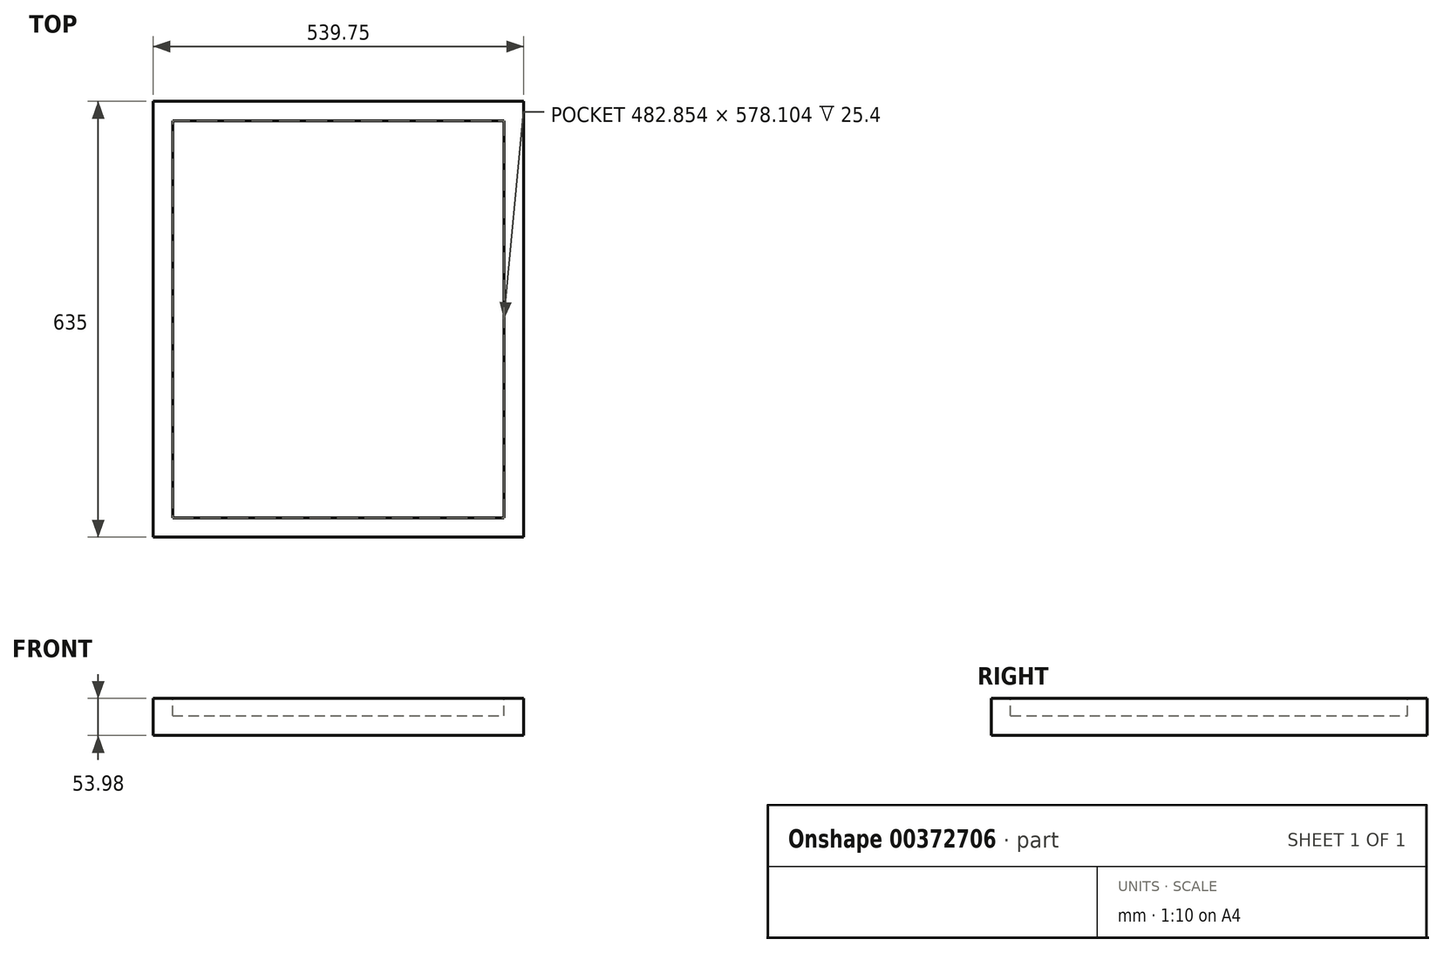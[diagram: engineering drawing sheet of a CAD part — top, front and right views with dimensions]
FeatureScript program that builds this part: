
annotation { "Feature Type Name" : "Feature", "Feature Type Description" : "" }
export const myFeature = defineFeature(function(context is Context, id is Id, definition is map)
    precondition{}
    {
        {
            var Q0;
            Q0=qCreatedBy(makeId("Front.planeOp"),FACE);
            var sketch = newSketch(context, id + "F0", { "sketchPlane" : qUnion([Q0])});
            skLineSegment(sketch, "E0.bottom", {"start": v(0, 0) * mm, "end": v(539.75, 0) * mm});
            skLineSegment(sketch, "E0.top", {"start": v(0, 53.98) * mm, "end": v(539.75, 53.98) * mm});
            skLineSegment(sketch, "E0.left", {"start": v(0, 0) * mm, "end": v(0, 53.98) * mm});
            skLineSegment(sketch, "E0.right", {"start": v(539.75, 0) * mm, "end": v(539.75, 53.98) * mm});
            skSolve(sketch);
        }
        {
            var Q0;
            Q0 = qSketchRegion(id + "F0", true);
            extrude(context, id + "F1", {"entities" : qUnion([Q0]), "oppositeDirection" : true, "depth" : 635 * mm});
        }
        {
            var Q0;
            Q0=makeQuery(id+"F1.opExtrude","SWEPT_FACE",FACE,{"disambiguationData":[OSD([sQuery(id+"F0.wireOp",EDGE,"E0.top")])]});
            var sketch = newSketch(context, id + "F2", { "sketchPlane" : qUnion([Q0])});
            skLineSegment(sketch, "E1.bottom", {"start": v(28.45, 28.45) * mm, "end": v(511.3, 28.45) * mm});
            skLineSegment(sketch, "E1.top", {"start": v(28.45, 606.55) * mm, "end": v(511.3, 606.55) * mm});
            skLineSegment(sketch, "E1.left", {"start": v(28.45, 28.45) * mm, "end": v(28.45, 606.55) * mm});
            skLineSegment(sketch, "E1.right", {"start": v(511.3, 28.45) * mm, "end": v(511.3, 606.55) * mm});
            skSolve(sketch);
        }
        {
            var Q0;
            Q0 = qSketchRegion(id + "F2", true);
            extrude(context, id + "F3", {"entities" : qUnion([Q0]), "operationType" : NewBodyOperationType.REMOVE, "oppositeDirection" : true, "depth" : 25.4 * mm});
        }
        {
            var Q0;
            Q0=makeQuery(id+"F1.opExtrude","SWEPT_FACE",FACE,{"disambiguationData":[OSD([sQuery(id+"F0.wireOp",EDGE,"E0.bottom")])]});
            var sketch = newSketch(context, id + "F4", { "sketchPlane" : qUnion([Q0])});
            skSolve(sketch);
        }
        {
            var Q0;
            Q0 = qSketchRegion(id + "F4", true);
            var Q1;
            Q1=makeQuery(id+"F1.opExtrude","SWEPT_FACE",FACE,{"disambiguationData":[OSD([sQuery(id+"F0.wireOp",EDGE,"E0.bottom")])]});
            extrude(context, id + "F5", {"entities" : qUnion([Q0, Q1]), "depth" : 28.57 * mm});
        }
        {
            var Q0;
            Q0=makeQuery(id+"F5.opExtrude","SWEPT_BODY",BODY,{"disambiguationData":[OSD([sQuery(id+"F0.wireOp",EDGE,"E0.bottom")])]});
            deleteBodies(context, id + "F6", {"entities" : qUnion([Q0])});
        }
    });
